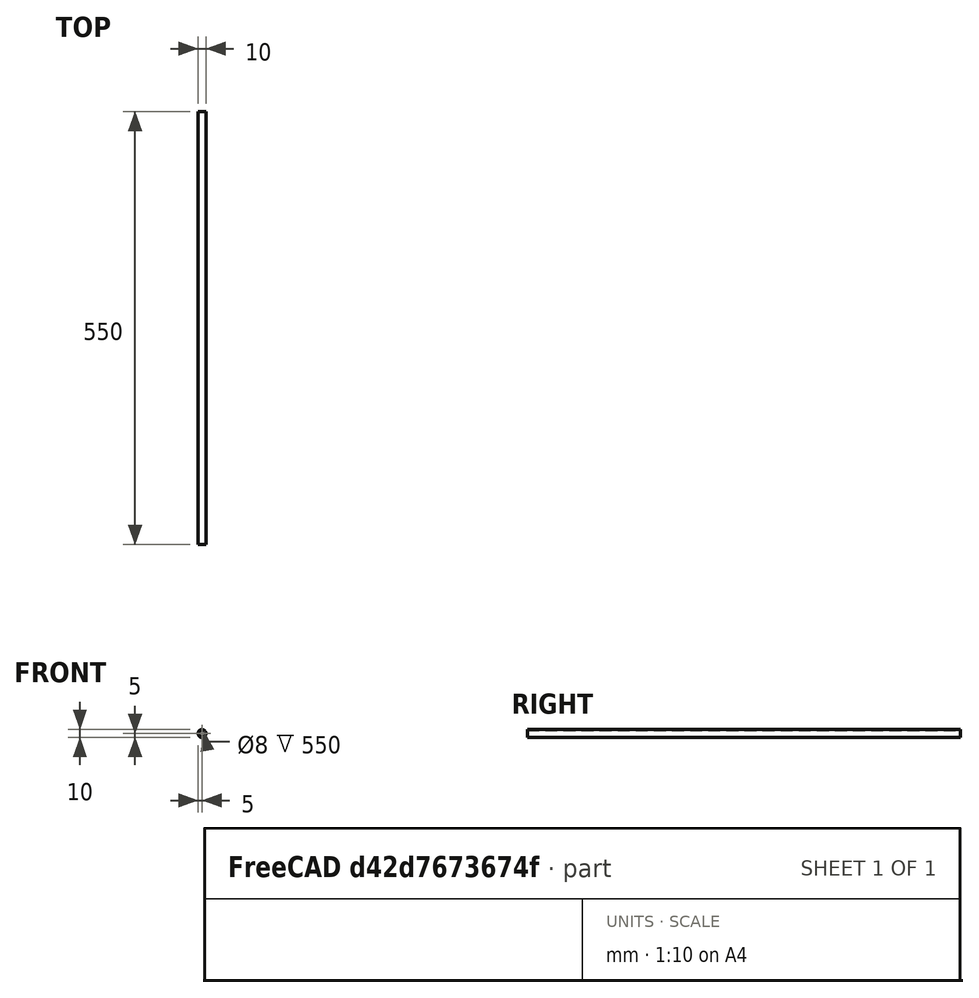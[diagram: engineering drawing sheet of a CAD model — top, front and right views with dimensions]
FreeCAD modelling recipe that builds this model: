
FCSTD DOCUMENT  (FreeCAD 0.19R23742 (Git))
Label: rod
License: All rights reserved
LicenseURL: http://en.wikipedia.org/wiki/All_rights_reserved
objects: Sketcher::SketchObject×1, PartDesign::Pad×1, PartDesign::Body×1
note: 4 computed .brp shape members not serialized (recipe doc carries the construction recipe); baked Part::Feature solids carry a one-line shape summary decoded from their .brp

FEATURE [Sketcher::SketchObject] Sketch
  FullyConstrained = true
  MapMode = 5
  Placement = pos=(0,0,0) rot=(1,0,0;1.5708rad)
  Support = -> [XZ_Plane]
  sketch-geometry (2):
    g0: Circle CenterX=0 CenterY=0 CenterZ=0 NormalX=0 NormalY=0 NormalZ=1 AngleXU=0 Radius=4
    g1: Circle CenterX=0 CenterY=0 CenterZ=0 NormalX=0 NormalY=0 NormalZ=1 AngleXU=0 Radius=5
  constraints (4):
    c: Coincident(g0,g-1)
    c: Coincident(g1,g0)
    c: Radius(g0) = 4
    c: Radius(g1) = 5
FEATURE [PartDesign::Pad] Pad
  Direction = (1,1,1)
  Length = 550
  Length2 = 100
  Placement = pos=(0,0,0) rot=(1,0,0;1.5708rad)
  Profile = -> Sketch
  Type = 0
FEATURE [PartDesign::Body] Body
  Group = -> [Sketch,Pad]
  Origin = -> Origin
  Tip = -> Pad
